# Revit family: 2019_ES_Ventana_Qsystems_Q77C16_1-Hoja
name_source: partatom
category: Windows
units: mm (PartAtom-declared; Revit-internal decimal feet)

## family parameters
Always vertical = Yes
Cut with Voids When Loaded = No
Host = Wall
OmniClass Number = 23.30.20.00
OmniClass Title = Windows
Room Calculation Point = No
Shared = No

## types (4) — shared parameters
Acabado = Anodizado, lacado y acabados
Acristalamiento = Cristal - Vidrio claro templado 6/12/6/12/6
Alto Vidrio = 1262 mm
Altura Real = 1480 mm
Altura de antepecho por defecto = 800 mm
Altura maxima = 2500 mm
Altura minima = 600 mm
Analytic Construction = <Ninguno>
Ancho Marco = 109 mm
Ancho P1 = 109 mm
Ancho Vidrio = 1012 mm
AnchoPoliamidaHoja = 24 mm
AnchoPoliamidaMarco = 24 mm
Anchura Maxima = 1700 mm
Anchura Minima = 600 mm
Anchura Real = 1230 mm
Area = 1.82 m²
Autor = Bimetica Parametric Design Services S.L.
BIMsupport = https://bimsupport.info
COBieCategoria = IfcWindow
Catálogo (URL) = https://qsystemsaluminio.com
CerramientoExterior = Yes
Clasificacion acustica = 45 (-2,-6) dB
ConfiguracionPoliamidas = 350300 - 479700 - 464700
Description = Ventana practicable/oscilobatiente de una hoja, de apertura interior
Desfase Exterior = 0 mm
Desfase Interior = 0 mm
Dist 1 = 92 mm
Espesor Perfiles Aluminio = 2 mm
EstanqueidadAgua = E2250
FechaEmisionElementoBIM = 03/12/2021
FechaVencimientoElementoBIM = 03/12/2022
Fraccion de area de acristalamiento = 0.701823
Grosor Acristalamiento = 42 mm
GrosorMarco = 70 mm
GrosorMaximoAcristalamiento = 52 mm
GrosorMinimoAcristalamiento = 0 mm
Gubimclass Codigo = 30.10.20.10
Gubimclass Titulo = Ventanas de fachadas
Height = 1480 mm
Historial = (RVT2019) Creación del Elemento.
IfcExportAs = IfcWindow
IfcExportType = Ventana Practicable
InformacionTecnica = https://qsystemsaluminio.com
Intercalario = Technoform Warm Edge
Manilla = Plástico, negro opaco
Manufacturer = QSystems
Marcado CE = No
Marco = Aluminio Anodizado, lacado
MasterformatCodigo = 08 51 13
MasterformatTitulo = Aluminum Windows
Motorizada = No
Numero de Licencia = XXX-XXXX9536
OmniclassCodigo = 23-17 13 13 15
OmniclassTitulo = Metal Single Hung Windows
Perimetro = 4192 mm
PermeabilidadAlAire = Clase 4
Peso = 0.00 kg
Plataforma descaga contenido BIM = www.bimetica.com
Poliamida = Technoform polyamide
Profundidad = 77 mm
PuntoDeContacto = QSystems
Referencia = Q77C16
ReferenciaContacto = QSystems
RepisaExterior = Yes
RepisaInterior = Yes
ResistenciaAlViento = C5
Rough Height = 1490 mm
Rough Width = 1240 mm
SalidaEmergencia = Yes
Serie = Q77C16
TelefonoContacto = +34 91 895 58 00
Titular = Alueuropa S.A.
Total Y𝑔 = 0.049
Total 𝐴𝑓 = 0.542801
Total 𝐴𝑔 = 1.277599
Total 𝑈𝑔 = 1.8
Total 𝑙𝑔 = 4.5488
UNSPSCCodigo = 30171606
UNSPSCTitulo = Casement windows
URL = https://qsystemsaluminio.com
URL Perfil BIM = https://bimetica.com
URL Poliamida = http://www.technoform.es
URL Poliamida - Catálogo = http://www.technoform.com
URLProducto = https://qsystemsaluminio.com
Uniclass2.0Codigo = 25-30-95-88
Uniclass2.0Titulo = Tilt-and-turn window systems
Version = RVT2019
Version Estandar GDO-BIM = GDO-BIM V02
Wall Closure = Both
Width = 1230 mm
Y𝑔 P1 = 0.049
𝐴𝑓 P1 = 0.54 m²
𝐴𝑔 V1 = 1.28 m²
𝑈𝑔 V1 = 1.8
𝑙𝑔 P1 = 4.5488
zero-valued in all types: AcidificacionAtmosfericaPorUnidad, AguaConsumidaPorUnidad, CambioClimaticoPorUnidad, CosteMantenimiento, DestruccionCapaOzonoEstratosfericaPorUnidad, Energia consumida, EnergiaNoRenovableConsumidaPorUnidad, EnergiaPrimariaTotalConsumidaPorUnidad, EnergiaRenovableConsumidaPorUnidad, EutrofizacionPorUnidad, FaltaDeRecursosPorUnidad, FormacionFotoquimicaOzonoPorUnidad, Infiltracion, ResiduoInertePorUnidad, ResiduoRadioactivoPorUnidad, ResiduosNoPeligrososPorUnidad, ResiduosPeligrososPorUnidad

## per-type parameters (varying)
| type | ControlHumos | Espuma | Heat Transfer Coefficient (U) | Model | Operation | Oscilobatiente | Practicable | Total 𝑈𝑓 | Transmitancia termica | 𝑈𝑓 P1 | 𝑈𝑤 |
| 1230 x 1480 mm - Oscilobatiente | Yes |  | 2.161 W/(m²·K) | Ventana Q77C16 - 1 Hoja Oscilobatiente | Oscilobatiente | Yes | No | 2.6 | 2.161 W/(m²·K) | 2.6 | 2.160982 |
| 1230 x 1480 mm - Practicable | No |  | 2.161 W/(m²·K) | Ventana Q77C16 - 1 Hoja Practicable | Practicable | No | Yes | 2.6 | 2.161 W/(m²·K) | 2.6 | 2.160982 |
| 1230 x 1480 mm - Oscilobatiente, con Espuma | No | Espuma de conductividad 0.021W/mK entre varillas.
Espuma de conductividad 0.034W/mK en el galce del vidrio y en el marco. | 1.9821 W/(m²·K) | Ventana Q77C16 - 1 Hoja Oscilobatiente | Oscilobatiente | Yes | No | 2 | 1.9821 W/(m²·K) | 2 | 1.982076 |
| 1230 x 1480 mm - Practicable, con Espuma | No | Espuma de conductividad 0.021W/mK entre varillas.
Espuma de conductividad 0.034W/mK en el galce del vidrio y en el marco. | 1.9821 W/(m²·K) | Ventana Q77C16 - 1 Hoja Practicable | Practicable | No | Yes | 2 | 1.9821 W/(m²·K) | 2 | 1.982076 |

## geometry (parser evidence)
native form markers: Blend x2
no freeform markers — native parametric forms only
